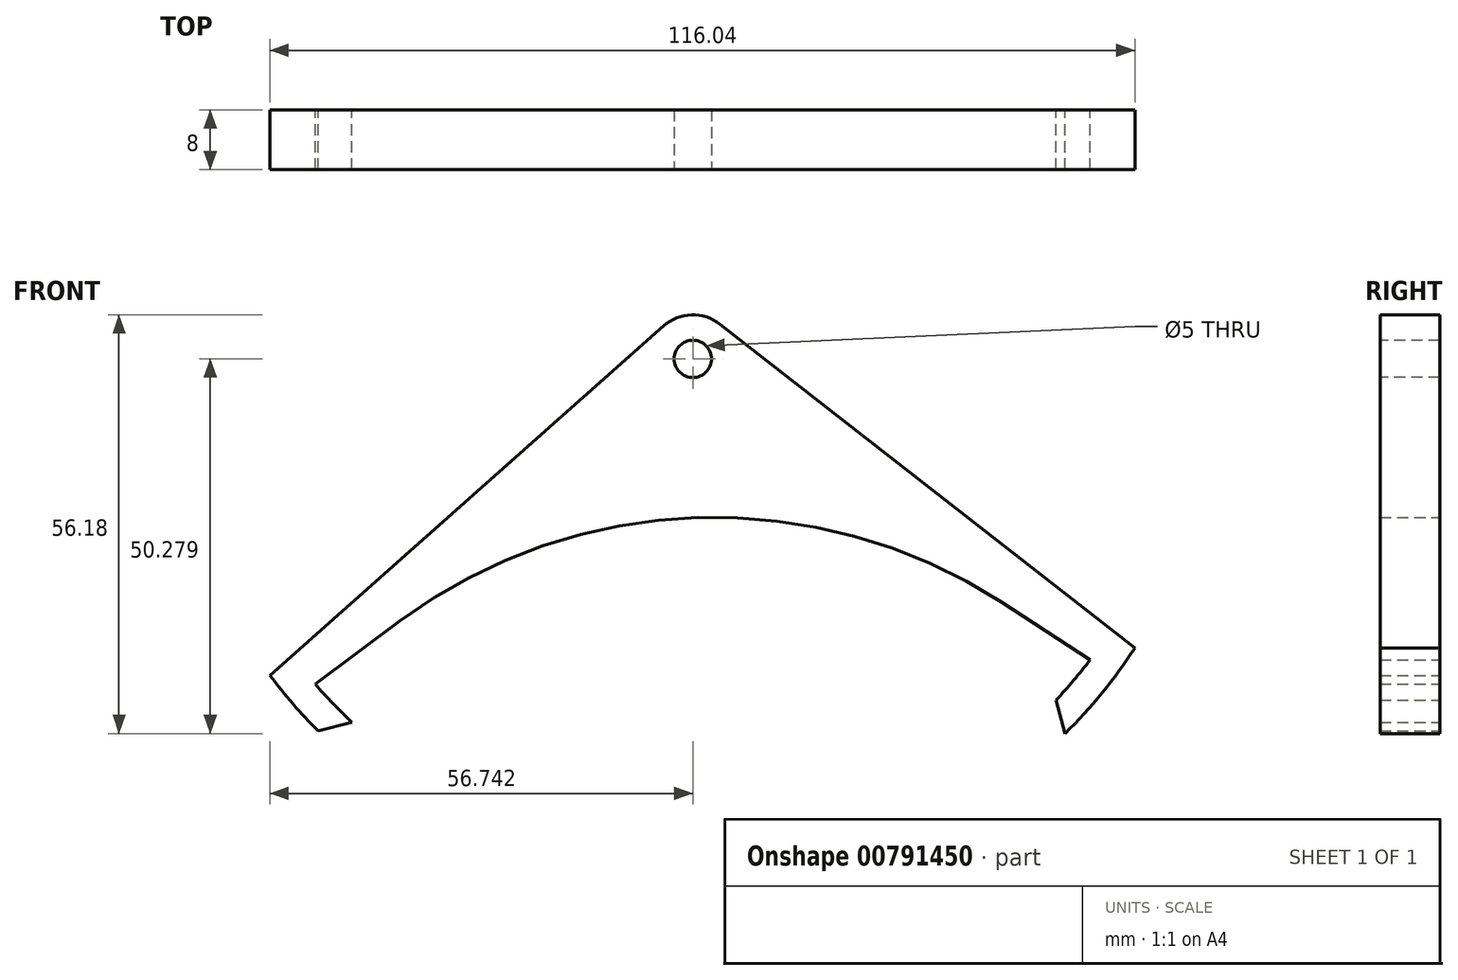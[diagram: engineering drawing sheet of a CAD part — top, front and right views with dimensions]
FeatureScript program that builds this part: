
annotation { "Feature Type Name" : "Feature", "Feature Type Description" : "" }
export const myFeature = defineFeature(function(context is Context, id is Id, definition is map)
    precondition{}
    {
        {
            var Q0;
            Q0=qCreatedBy(makeId("Front.planeOp"),FACE);
            var sketch = newSketch(context, id + "F0", { "sketchPlane" : qUnion([Q0])});
            skLineSegment(sketch, "E0", {"start": v(-51.56, -27.75) * mm, "end": v(-47.05, -26.56) * mm});
            skLineSegment(sketch, "E1", {"start": v(48.66, -28.1) * mm, "end": v(47.47, -23.58) * mm});
            skArc(sketch, "E2", {"start": v(-58.02, -20.26) * mm, "mid": v(-54.92, -24.12) * mm, "end": v(-51.56, -27.75) * mm});
            skArc(sketch, "E3", {"start": v(-51.95, -21.44) * mm, "mid": v(-49.57, -24.06) * mm, "end": v(-47.05, -26.56) * mm});
            skLineSegment(sketch, "E4", {"start": v(58.02, -16.61) * mm, "end": v(2.36, 26.84) * mm});
            skLineSegment(sketch, "E5", {"start": v(-58.02, -20.26) * mm, "end": v(-5.2, 26.6) * mm});
            skLineSegment(sketch, "E6", {"start": v(52.04, -18.17) * mm, "end": v(40.18, -10.48) * mm});
            skLineSegment(sketch, "E7", {"start": v(-51.95, -21.44) * mm, "end": v(-40.6, -13.02) * mm});
            skArc(sketch, "E8", {"start": v(48.66, -28.1) * mm, "mid": v(53.64, -22.6) * mm, "end": v(58.02, -16.61) * mm});
            skArc(sketch, "E9", {"start": v(47.47, -23.58) * mm, "mid": v(49.82, -20.93) * mm, "end": v(52.04, -18.17) * mm});
            skArc(sketch, "E10", {"start": v(40.18, -10.48) * mm, "mid": v(-0.6, 0.9) * mm, "end": v(-40.6, -13.02) * mm});
            skArc(sketch, "E11", {"start": v(2.36, 26.84) * mm, "mid": v(-1.46, 28.1) * mm, "end": v(-5.2, 26.6) * mm});
            skSolve(sketch);
        }
        {
            var Q0;
            Q0=makeQuery(id+"F0.imprint","IMPRINT",FACE,{"disambiguationData":[TD([[makeQuery(id+"F0.imprint","IMPRINT",EDGE,{"derivedFrom":sQuery(id+"F0.wireOp",EDGE,"E0")}),1.0]])]});
            extrude(context, id + "F1", {"entities" : qUnion([Q0]), "depth" : 8 * mm, "offsetDistance" : 25 * mm});
        }
        {
            var Q0;
            Q0=makeQuery(id+"F1.opExtrude","CAP_FACE",FACE,{"disambiguationData":[OSD([sQuery(id+"F0.wireOp",EDGE,"E0"),sQuery(id+"F0.wireOp",EDGE,"E1"),sQuery(id+"F0.wireOp",EDGE,"E2"),sQuery(id+"F0.wireOp",EDGE,"E3"),sQuery(id+"F0.wireOp",EDGE,"E4"),sQuery(id+"F0.wireOp",EDGE,"E5"),sQuery(id+"F0.wireOp",EDGE,"E6"),sQuery(id+"F0.wireOp",EDGE,"E7"),sQuery(id+"F0.wireOp",EDGE,"E8"),sQuery(id+"F0.wireOp",EDGE,"E9"),sQuery(id+"F0.wireOp",EDGE,"E10"),sQuery(id+"F0.wireOp",EDGE,"E11")])],"isStart":false});
            var sketch = newSketch(context, id + "F2", { "sketchPlane" : qUnion([Q0])});
            skCircle(sketch, "E12", {"center": v(-1.28, 22.19) * mm, "radius": 2.5 * mm});
            skSolve(sketch);
        }
        {
            var Q0;
            Q0 = qSketchRegion(id + "F2", true);
            var Q1;
            Q1=sQuery(id+"F2.wireOp",EDGE,"E12");
            var Q2;
            Q2=makeQuery(id+"F1.opExtrude","SWEPT_BODY",BODY,{"disambiguationData":[OSD([sQuery(id+"F0.wireOp",EDGE,"E0"),sQuery(id+"F0.wireOp",EDGE,"E1"),sQuery(id+"F0.wireOp",EDGE,"E2"),sQuery(id+"F0.wireOp",EDGE,"E3"),sQuery(id+"F0.wireOp",EDGE,"E4"),sQuery(id+"F0.wireOp",EDGE,"E5"),sQuery(id+"F0.wireOp",EDGE,"E6"),sQuery(id+"F0.wireOp",EDGE,"E7"),sQuery(id+"F0.wireOp",EDGE,"E8"),sQuery(id+"F0.wireOp",EDGE,"E9"),sQuery(id+"F0.wireOp",EDGE,"E10"),sQuery(id+"F0.wireOp",EDGE,"E11")])]});
            extrude(context, id + "F3", {"entities" : qUnion([Q0]), "operationType" : NewBodyOperationType.REMOVE, "surfaceEntities" : qUnion([Q1]), "endBound" : BoundingType.UP_TO_BODY, "oppositeDirection" : true, "depth" : 25 * mm, "endBoundEntityBody" : qUnion([Q2]), "offsetDistance" : 25 * mm});
        }
    });
